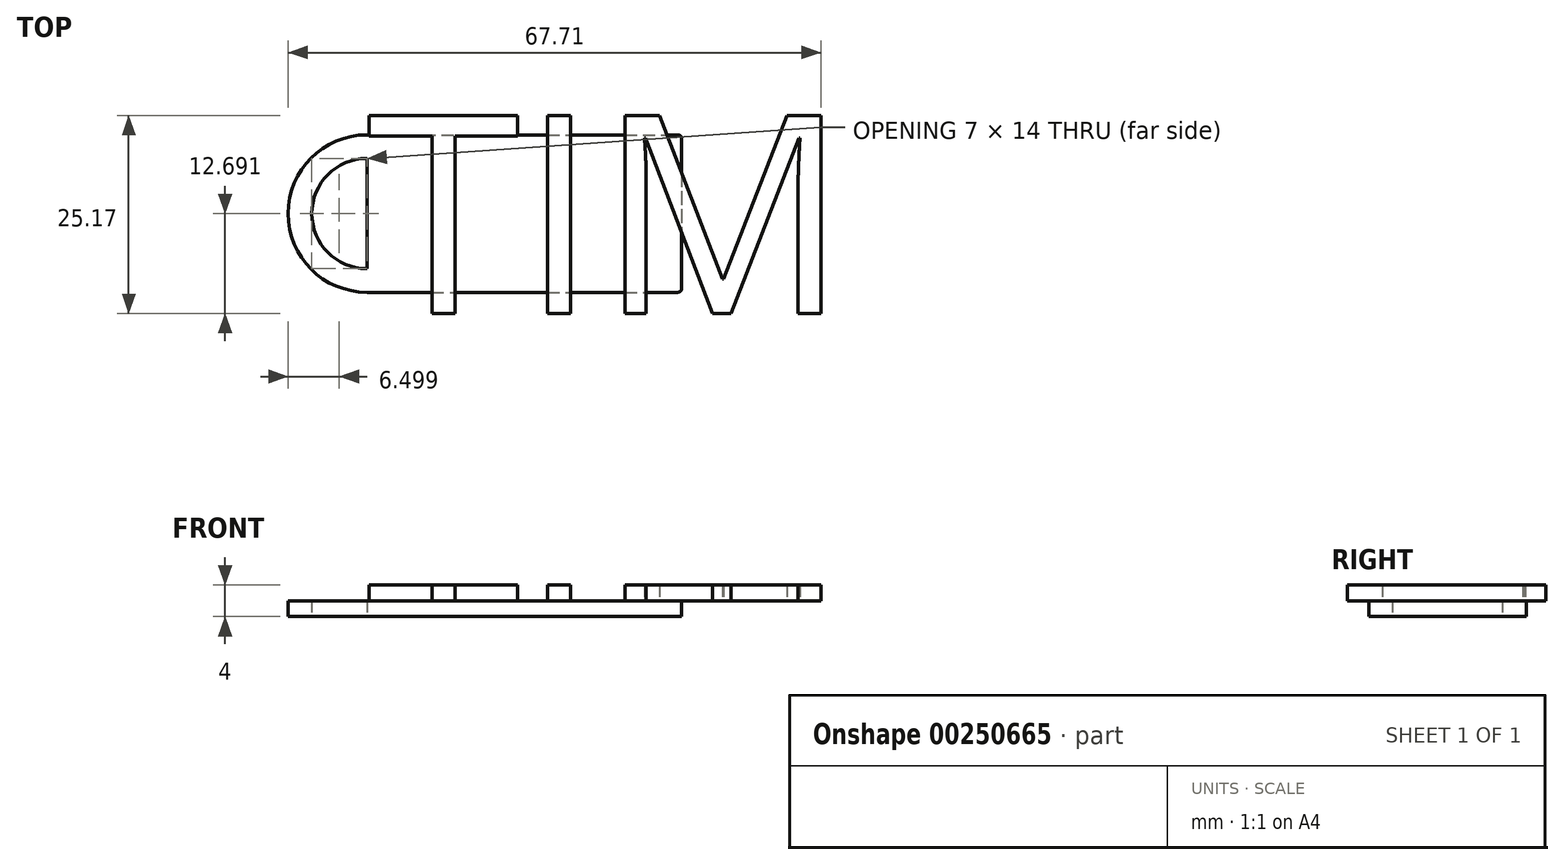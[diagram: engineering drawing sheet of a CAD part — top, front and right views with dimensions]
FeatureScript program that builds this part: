
annotation { "Feature Type Name" : "Feature", "Feature Type Description" : "" }
export const myFeature = defineFeature(function(context is Context, id is Id, definition is map)
    precondition{}
    {
        {
            var Q0;
            Q0=qCreatedBy(makeId("Top.planeOp"),FACE);
            var sketch = newSketch(context, id + "F0", { "sketchPlane" : qUnion([Q0])});
            skLineSegment(sketch, "E0.bottom", {"start": v(-5.27, 3.22) * mm, "end": v(34.73, 3.22) * mm});
            skLineSegment(sketch, "E0.top", {"start": v(-5.27, -16.78) * mm, "end": v(34.73, -16.78) * mm});
            skLineSegment(sketch, "E0.left", {"start": v(-5.27, 3.22) * mm, "end": v(-5.27, -16.78) * mm});
            skLineSegment(sketch, "E0.right", {"start": v(34.73, 3.22) * mm, "end": v(34.73, -16.78) * mm});
            skArc(sketch, "E1", {"start": v(-5.27, 3.22) * mm, "mid": v(-15.27, -6.78) * mm, "end": v(-5.27, -16.78) * mm});
            skArc(sketch, "E2", {"start": v(-5.27, 0.22) * mm, "mid": v(-12.27, -6.78) * mm, "end": v(-5.27, -13.78) * mm});
            skSolve(sketch);
        }
        {
            var Q0;
            Q0=qSketchRegion(id+"F0",true);
            extrude(context, id + "F4", {"entities" : qUnion([Q0]), "flatOperationType" : FlatOperationType.REMOVE, "offsetDistance" : 25 * mm, "depth" : 2 * mm, "domain" : OperationDomain.MODEL});
        }
        {
            var Q0;
            Q0=makeQuery(id+"F4.opExtrude","SWEPT_EDGE",EDGE,{"disambiguationData":[OSD([sQuery(id+"F0.wireOp",EDGE,"E0.top"),sQuery(id+"F0.wireOp",EDGE,"E0.right")])]});
            var Q1;
            Q1=makeQuery(id+"F4.opExtrude","SWEPT_EDGE",EDGE,{"disambiguationData":[OSD([sQuery(id+"F0.wireOp",EDGE,"E0.bottom"),sQuery(id+"F0.wireOp",EDGE,"E0.right")])]});
            fillet(context, id + "F1", {"entities" : qUnion([Q0, Q1]), "radius" : 0.5 * mm, "tangentPropagation" : true, "allowEdgeOverflow" : false});
        }
        {
            var Q0;
            Q0=makeQuery(id+"F4.opExtrude","CAP_FACE",FACE,{"disambiguationData":[OSD([sQuery(id+"F0.wireOp",EDGE,"E0.bottom"),sQuery(id+"F0.wireOp",EDGE,"E0.top"),sQuery(id+"F0.wireOp",EDGE,"E0.left"),sQuery(id+"F0.wireOp",EDGE,"E0.right"),sQuery(id+"F0.wireOp",EDGE,"E1"),sQuery(id+"F0.wireOp",EDGE,"E2")])],"isStart":false});
            var sketch = newSketch(context, id + "F2", { "sketchPlane" : qUnion([Q0]), "disableImprinting" : false});
            skText(sketch, "E3", { "text": "TIM", "fontName": "OpenSans-Regular.ttf"});
            skPoint(sketch, "E4", {"position": v(-5.27, -6.78) * mm});
            skPoint(sketch, "E5", {"position": v(34.73, -6.78) * mm});
            const initialGuessF2  = {"E3": [-0.00527, -0.01947, 1, 0, 0.02538]};
            skSetInitialGuess(sketch, initialGuessF2);
            skSolve(sketch);
        }
        {
            var Q0;
            Q0 = qSketchRegion(id + "F2", true);
            extrude(context, id + "F3", {"entities" : qUnion([Q0]), "operationType" : NewBodyOperationType.ADD, "flatOperationType" : FlatOperationType.REMOVE, "offsetDistance" : 25 * mm, "depth" : 2 * mm, "domain" : OperationDomain.MODEL});
        }
    });
